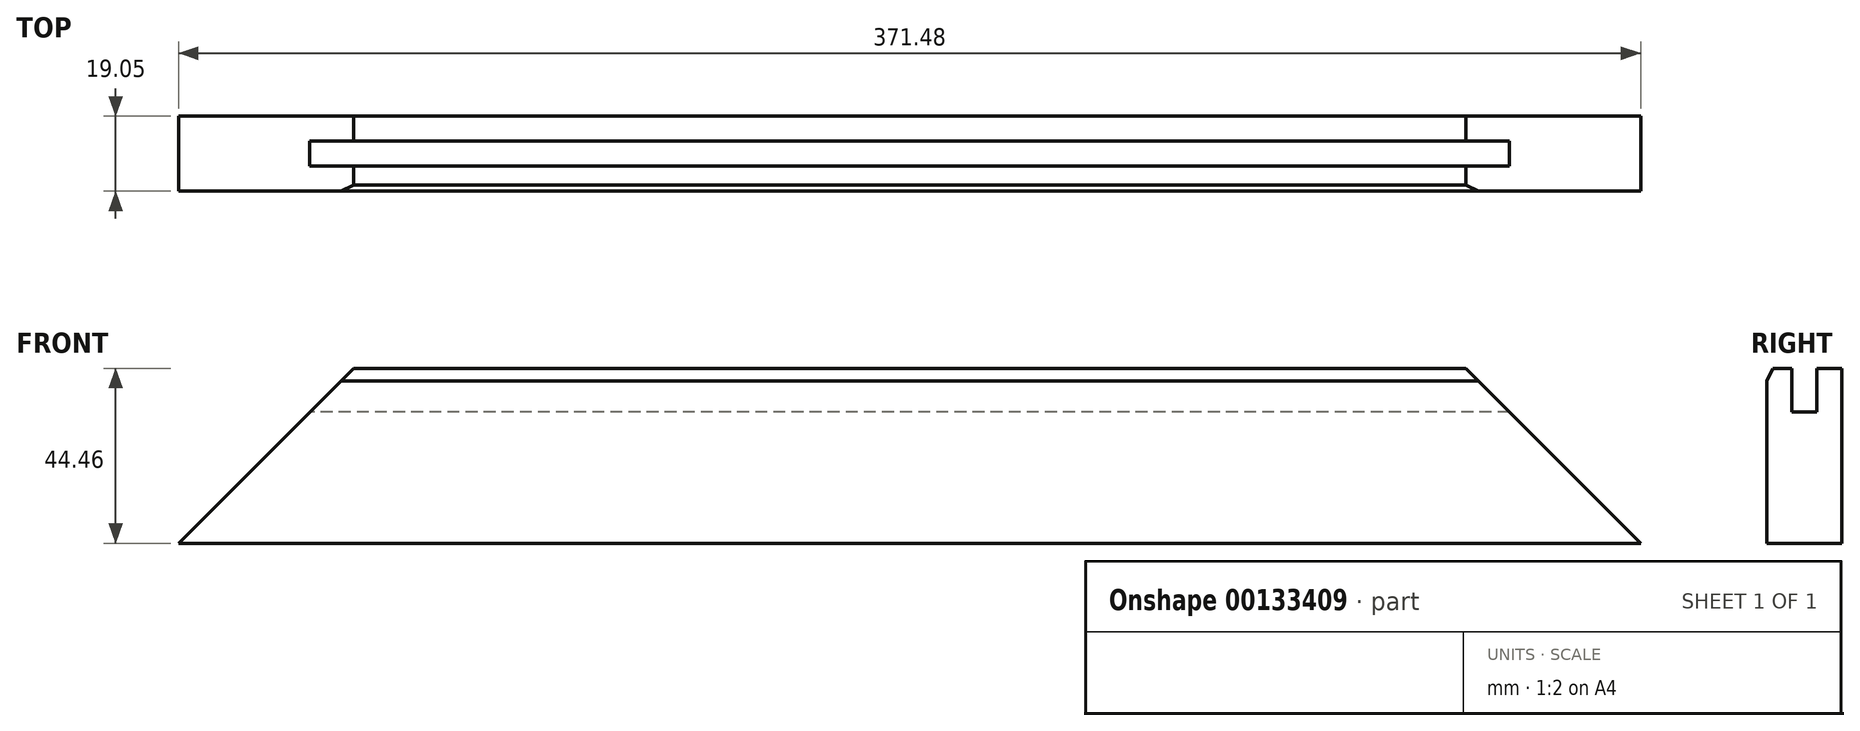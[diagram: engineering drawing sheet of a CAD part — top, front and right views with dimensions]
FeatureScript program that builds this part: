
annotation { "Feature Type Name" : "Feature", "Feature Type Description" : "" }
export const myFeature = defineFeature(function(context is Context, id is Id, definition is map)
    precondition{}
    {
        {
            var Q0;
            Q0=qCreatedBy(makeId("Front.planeOp"),FACE);
            var sketch = newSketch(context, id + "F0", { "sketchPlane" : qUnion([Q0])});
            skLineSegment(sketch, "E0.bottom", {"start": v(-185.74, 22.22) * mm, "end": v(185.74, 22.22) * mm});
            skLineSegment(sketch, "E0.top", {"start": v(-185.74, -22.22) * mm, "end": v(185.74, -22.22) * mm});
            skLineSegment(sketch, "E0.left", {"start": v(-185.74, 22.22) * mm, "end": v(-185.74, -22.22) * mm});
            skLineSegment(sketch, "E0.right", {"start": v(185.74, 22.22) * mm, "end": v(185.74, -22.22) * mm});
            skPoint(sketch, "E0.middle", {"position": v(0, 0) * mm});
            skLineSegment(sketch, "E1", {"start": v(-185.74, -22.22) * mm, "end": v(-141.29, 22.22) * mm, "construction": true});
            skLineSegment(sketch, "E2", {"start": v(185.74, -22.22) * mm, "end": v(141.29, 22.23) * mm, "construction": true});
            skLineSegment(sketch, "E3", {"start": v(-152.4, 11.11) * mm, "end": v(-185.74, 11.11) * mm, "construction": true});
            skLineSegment(sketch, "E4", {"start": v(185.74, 11.11) * mm, "end": v(152.4, 11.11) * mm, "construction": true});
            skSolve(sketch);
        }
        {
            var Q0;
            Q0=qSketchRegion(id+"F0",true);
            extrude(context, id + "F1", {"entities" : qUnion([Q0]), "depth" : 19.05 * mm});
        }
        {
            var Q0;
            Q0=makeQuery(id+"F1.opExtrude","SWEPT_FACE",FACE,{"disambiguationData":[OSD([sQuery(id+"F0.wireOp",EDGE,"E0.left")])]});
            var sketch = newSketch(context, id + "F2", { "sketchPlane" : qUnion([Q0])});
            skLineSegment(sketch, "E5", {"start": v(9.53, 22.22) * mm, "end": v(9.53, -22.23) * mm, "construction": true});
            skLineSegment(sketch, "E6.bottom", {"start": v(6.35, 22.22) * mm, "end": v(12.7, 22.22) * mm});
            skLineSegment(sketch, "E6.top", {"start": v(6.35, 11.11) * mm, "end": v(12.7, 11.11) * mm});
            skLineSegment(sketch, "E6.left", {"start": v(6.35, 22.22) * mm, "end": v(6.35, 11.11) * mm});
            skLineSegment(sketch, "E6.right", {"start": v(12.7, 22.22) * mm, "end": v(12.7, 11.11) * mm});
            skSolve(sketch);
        }
        {
            var Q0;
            Q0=qSketchRegion(id+"F2",true);
            extrude(context, id + "F3", {"entities" : qUnion([Q0]), "operationType" : NewBodyOperationType.REMOVE, "endBound" : BoundingType.THROUGH_ALL, "oppositeDirection" : true, "depth" : 25.4 * mm});
        }
        {
            var Q0;
            Q0=makeQuery(id+"F1.opExtrude","CAP_EDGE",EDGE,{"disambiguationData":[OSD([sQuery(id+"F0.wireOp",EDGE,"E0.bottom")])],"isStart":false});
            chamfer(context, id + "F4", {"entities" : qUnion([Q0]), "chamferType" : ChamferType.TWO_OFFSETS, "width1" : 1.59 * mm, "oppositeDirection" : false, "width2" : 3.17 * mm, "tangentPropagation" : true});
        }
        {
            var Q0;
            Q0=makeQuery(id+"F1.opExtrude","CAP_FACE",FACE,{"disambiguationData":[OSD([sQuery(id+"F0.wireOp",EDGE,"E0.bottom"),sQuery(id+"F0.wireOp",EDGE,"E0.top"),sQuery(id+"F0.wireOp",EDGE,"E0.left"),sQuery(id+"F0.wireOp",EDGE,"E0.right")])],"isStart":true});
            var sketch = newSketch(context, id + "F5", { "sketchPlane" : qUnion([Q0])});
            skLineSegment(sketch, "E7", {"start": v(-185.74, -22.23) * mm, "end": v(-141.29, 22.22) * mm});
            skLineSegment(sketch, "E8", {"start": v(-141.29, 22.22) * mm, "end": v(-185.74, 22.22) * mm});
            skLineSegment(sketch, "E9", {"start": v(-185.74, 22.22) * mm, "end": v(-185.74, -22.22) * mm});
            skLineSegment(sketch, "E10", {"start": v(0, 22.22) * mm, "end": v(0, -22.22) * mm, "construction": true});
            skLineSegment(sketch, "E11.MirrorCS", {"start": v(185.74, -22.22) * mm, "end": v(141.29, 22.23) * mm});
            skLineSegment(sketch, "E12.MirrorCS", {"start": v(185.74, 22.22) * mm, "end": v(185.74, -22.22) * mm});
            skLineSegment(sketch, "E13.MirrorCS", {"start": v(141.29, 22.22) * mm, "end": v(185.74, 22.22) * mm});
            skSolve(sketch);
        }
        {
            var Q0;
            Q0 = qSketchRegion(id + "F5", true);
            extrude(context, id + "F6", {"entities" : qUnion([Q0]), "operationType" : NewBodyOperationType.REMOVE, "endBound" : BoundingType.THROUGH_ALL, "oppositeDirection" : true, "depth" : 25.4 * mm});
        }
    });
